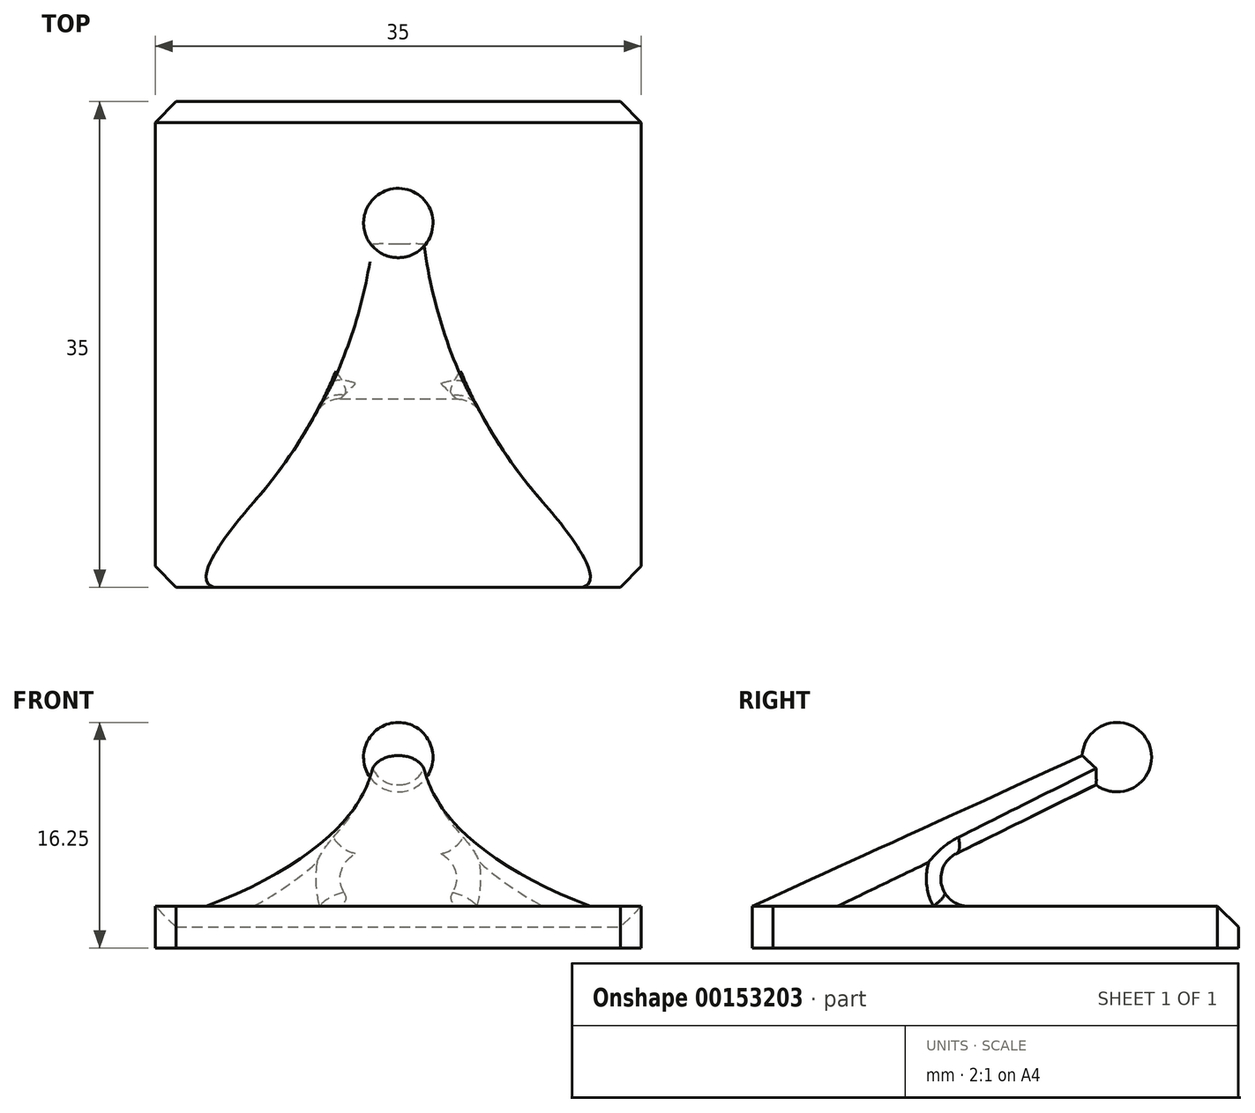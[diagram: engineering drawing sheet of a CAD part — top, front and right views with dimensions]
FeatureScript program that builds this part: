
annotation { "Feature Type Name" : "Feature", "Feature Type Description" : "" }
export const myFeature = defineFeature(function(context is Context, id is Id, definition is map)
    precondition{}
    {
        {
            assignVariable(context, id + "F0", {"name" : "base_width", "anyValue" : 35 * mm});
        }
        {
            var Q0;
            Q0=qCreatedBy(makeId("Right.planeOp"),FACE);
            var sketch = newSketch(context, id + "F1", { "sketchPlane" : qUnion([Q0])});
            skLineSegment(sketch, "E0", {"start": v(-17.5, 0) * mm, "end": v(17.5, 0) * mm});
            skLineSegment(sketch, "E1", {"start": v(17.5, 0) * mm, "end": v(17.5, 3) * mm});
            skLineSegment(sketch, "E2", {"start": v(17.5, 3) * mm, "end": v(-10.5, 3) * mm});
            skLineSegment(sketch, "E3", {"start": v(8.75, 15) * mm, "end": v(-17.5, 3) * mm});
            skLineSegment(sketch, "E4", {"start": v(-17.5, 3) * mm, "end": v(-17.5, 0) * mm});
            skPoint(sketch, "E5", {"position": v(0, 0) * mm});
            skLineSegment(sketch, "E6", {"start": v(-10.5, 3) * mm, "end": v(8.75, 12.5) * mm});
            skLineSegment(sketch, "E7", {"start": v(8.75, 12.5) * mm, "end": v(8.75, 15) * mm});
            skPoint(sketch, "E8", {"position": v(8.75, 13.75) * mm});
            skSolve(sketch);
        }
        {
            var Q0;
            Q0=qCreatedBy(makeId("Right.planeOp"),FACE);
            var sketch = newSketch(context, id + "F2", { "sketchPlane" : qUnion([Q0])});
            skPoint(sketch, "E9.0", {"position": v(8.75, 13.75) * mm});
            skLineSegment(sketch, "E10.0", {"start": v(8.75, 12.5) * mm, "end": v(8.75, 15) * mm, "construction": true});
            skLineSegment(sketch, "E11", {"start": v(8.75, 16.25) * mm, "end": v(8.75, 11.25) * mm});
            skArc(sketch, "E12", {"start": v(8.75, 11.25) * mm, "mid": v(11.25, 13.75) * mm, "end": v(8.75, 16.25) * mm});
            skSolve(sketch);
        }
        {
            var Q0;
            Q0 = qSketchRegion(id + "F1", true);
            extrude(context, id + "F3", {"entities" : qUnion([Q0]), "depth" : getVariable(context, 'base_width'), "symmetric" : true});
        }
        {
            var Q0;
            Q0=makeQuery(id+"F3.opExtrude","SWEPT_FACE",FACE,{"disambiguationData":[OSD([sQuery(id+"F1.wireOp",EDGE,"E2")])]});
            var sketch = newSketch(context, id + "F4", { "sketchPlane" : qUnion([Q0])});
            skPoint(sketch, "E13.0", {"position": v(0, -17.5) * mm});
            skPoint(sketch, "E14.0", {"position": v(0, 17.5) * mm});
            skPoint(sketch, "E15.0", {"position": v(0, 8.75) * mm});
            skLineSegment(sketch, "E16.bottom", {"start": v(-17.5, 17.5) * mm, "end": v(17.5, 17.5) * mm});
            skLineSegment(sketch, "E16.top", {"start": v(-17.5, -17.5) * mm, "end": v(17.5, -17.5) * mm});
            skLineSegment(sketch, "E16.left", {"start": v(-17.5, 17.5) * mm, "end": v(-17.5, -17.5) * mm});
            skLineSegment(sketch, "E16.right", {"start": v(17.5, 17.5) * mm, "end": v(17.5, -17.5) * mm});
            skLineSegment(sketch, "E17", {"start": v(1.87, 8.75) * mm, "end": v(-1.87, 8.75) * mm});
            skArc(sketch, "E18", {"start": v(-17.5, -17.5) * mm, "mid": v(-6.64, -6.2) * mm, "end": v(-1.87, 8.75) * mm});
            skArc(sketch, "E19", {"start": v(1.87, 8.75) * mm, "mid": v(6.64, -6.2) * mm, "end": v(17.5, -17.5) * mm});
            skLineSegment(sketch, "E20", {"start": v(-36.4, 11.53) * mm, "end": v(36.4, 11.53) * mm, "construction": true});
            skSolve(sketch);
        }
        {
            var Q0;
            {var subQ0=sQuery(id+"F4.wireOp",EDGE,"E16.left");var subQ1=makeQuery(id+"F3.opExtrude","SWEPT_EDGE",EDGE,{"disambiguationData":[OSD([sQuery(id+"F1.wireOp",EDGE,"E2"),sQuery(id+"F1.wireOp",EDGE,"E6")])]});var subQ2=makeQuery(id+"F4.imprint","INTERSECT",VERTEX,{"derivedFrom":[subQ1,subQ0]});Q0=makeQuery(id+"F4.imprint","IMPRINT",FACE,{"disambiguationData":[TD([[makeQuery(id+"F4.imprint","IMPRINT",EDGE,{"disambiguationData":[TD([[subQ2,-1.0]])],"derivedFrom":subQ0}),1.0]])]});}
            var Q1;
            {var subQ0=sQuery(id+"F4.wireOp",EDGE,"E16.right");var subQ1=makeQuery(id+"F3.opExtrude","SWEPT_EDGE",EDGE,{"disambiguationData":[OSD([sQuery(id+"F1.wireOp",EDGE,"E2"),sQuery(id+"F1.wireOp",EDGE,"E6")])]});var subQ2=makeQuery(id+"F4.imprint","INTERSECT",VERTEX,{"derivedFrom":[subQ1,subQ0]});Q1=makeQuery(id+"F4.imprint","IMPRINT",FACE,{"disambiguationData":[TD([[makeQuery(id+"F4.imprint","IMPRINT",EDGE,{"disambiguationData":[TD([[subQ2,-1.0]])],"derivedFrom":subQ0}),-1.0]])]});}
            var Q2;
            {var subQ2=sQuery(id+"F4.wireOp",EDGE,"E16.bottom");Q2=makeQuery(id+"F4.imprint","IMPRINT",FACE,{"disambiguationData":[TD([[makeQuery(id+"F4.imprint","IMPRINT",EDGE,{"derivedFrom":subQ2}),1.0]])]});}
            extrude(context, id + "F5", {"entities" : qUnion([Q0, Q1, Q2]), "operationType" : NewBodyOperationType.REMOVE, "endBound" : BoundingType.THROUGH_ALL, "depth" : 25 * mm});
        }
        {
            var Q0;
            Q0=makeQuery(id+"F3.opExtrude","SWEPT_EDGE",EDGE,{"disambiguationData":[OSD([sQuery(id+"F1.wireOp",EDGE,"E2"),sQuery(id+"F1.wireOp",EDGE,"E6")])]});
            fillet(context, id + "F6", {"entities" : qUnion([Q0]), "radius" : 2 * mm, "tangentPropagation" : true, "allowEdgeOverflow" : false});
        }
        {
            var Q0;
            Q0=makeQuery(id+"F5.boolean.opBoolean","INTERSECT",EDGE,{"derivedFrom":[makeQuery(id+"F3.opExtrude","SWEPT_FACE",FACE,{"disambiguationData":[OSD([sQuery(id+"F1.wireOp",EDGE,"E3")])]}),makeQuery(id+"F5.opExtrude","SWEPT_FACE",FACE,{"disambiguationData":[OSD([sQuery(id+"F4.wireOp",EDGE,"E19")])]})]});
            var Q1;
            Q1=makeQuery(id+"F5.boolean.opBoolean","INTERSECT",EDGE,{"derivedFrom":[makeQuery(id+"F3.opExtrude","SWEPT_FACE",FACE,{"disambiguationData":[OSD([sQuery(id+"F1.wireOp",EDGE,"E3")])]}),makeQuery(id+"F5.opExtrude","SWEPT_FACE",FACE,{"disambiguationData":[OSD([sQuery(id+"F4.wireOp",EDGE,"E18")])]})]});
            var Q2;
            Q2=makeQuery(id+"F5.boolean.opBoolean","INTERSECT",EDGE,{"derivedFrom":[makeQuery(id+"F3.opExtrude","SWEPT_FACE",FACE,{"disambiguationData":[OSD([sQuery(id+"F1.wireOp",EDGE,"E6")])]}),makeQuery(id+"F5.opExtrude","SWEPT_FACE",FACE,{"disambiguationData":[OSD([sQuery(id+"F4.wireOp",EDGE,"E18")])]})]});
            var Q3;
            Q3=makeQuery(id+"F5.boolean.opBoolean","INTERSECT",EDGE,{"derivedFrom":[makeQuery(id+"F3.opExtrude","SWEPT_FACE",FACE,{"disambiguationData":[OSD([sQuery(id+"F1.wireOp",EDGE,"E6")])]}),makeQuery(id+"F5.opExtrude","SWEPT_FACE",FACE,{"disambiguationData":[OSD([sQuery(id+"F4.wireOp",EDGE,"E19")])]})]});
            fillet(context, id + "F7", {"entities" : qUnion([Q0, Q1, Q2, Q3]), "radius" : 2 * mm, "tangentPropagation" : true, "allowEdgeOverflow" : false});
        }
        {
            var Q0;
            Q0=makeQuery(id+"F5.boolean.opBoolean","MERGE",EDGE,{"derivedFrom":[makeQuery(id+"F3.opExtrude","CAP_EDGE",EDGE,{"disambiguationData":[OSD([sQuery(id+"F1.wireOp",EDGE,"E2")])],"isStart":true}),makeQuery(id+"F5.opExtrude","CAP_EDGE",EDGE,{"disambiguationData":[OSD([sQuery(id+"F4.wireOp",EDGE,"E16.left")])],"isStart":true})]});
            var Q1;
            Q1=makeQuery(id+"F3.opExtrude","SWEPT_EDGE",EDGE,{"disambiguationData":[OSD([sQuery(id+"F1.wireOp",EDGE,"E1"),sQuery(id+"F1.wireOp",EDGE,"E2")])]});
            var Q2;
            Q2=makeQuery(id+"F5.boolean.opBoolean","MERGE",EDGE,{"derivedFrom":[makeQuery(id+"F3.opExtrude","CAP_EDGE",EDGE,{"disambiguationData":[OSD([sQuery(id+"F1.wireOp",EDGE,"E2")])],"isStart":false}),makeQuery(id+"F5.opExtrude","CAP_EDGE",EDGE,{"disambiguationData":[OSD([sQuery(id+"F4.wireOp",EDGE,"E16.right")])],"isStart":true})]});
            var Q3;
            Q3=makeQuery(id+"F3.opExtrude","CAP_EDGE",EDGE,{"disambiguationData":[OSD([sQuery(id+"F1.wireOp",EDGE,"E4")])],"isStart":false});
            var Q4;
            Q4=makeQuery(id+"F3.opExtrude","CAP_EDGE",EDGE,{"disambiguationData":[OSD([sQuery(id+"F1.wireOp",EDGE,"E1")])],"isStart":false});
            var Q5;
            Q5=makeQuery(id+"F3.opExtrude","CAP_EDGE",EDGE,{"disambiguationData":[OSD([sQuery(id+"F1.wireOp",EDGE,"E1")])],"isStart":true});
            var Q6;
            Q6=makeQuery(id+"F3.opExtrude","CAP_EDGE",EDGE,{"disambiguationData":[OSD([sQuery(id+"F1.wireOp",EDGE,"E4")])],"isStart":true});
            chamfer(context, id + "F8", {"entities" : qUnion([Q0, Q1, Q2, Q3, Q4, Q5, Q6]), "width" : 1.5 * mm, "tangentPropagation" : true});
        }
        {
            var Q0;
            Q0=makeQuery(id+"F2.imprint","IMPRINT",FACE,{"disambiguationData":[TD([[makeQuery(id+"F2.imprint","IMPRINT",EDGE,{"derivedFrom":sQuery(id+"F2.wireOp",EDGE,"E11")}),1.0]])]});
            var Q1;
            Q1=sQuery(id+"F2.wireOp",EDGE,"E11");
            revolve(context, id + "F9", {"operationType" : NewBodyOperationType.ADD, "entities" : qUnion([Q0]), "axis" : qUnion([Q1]), "revolveType" : RevolveType.FULL});
        }
    });
